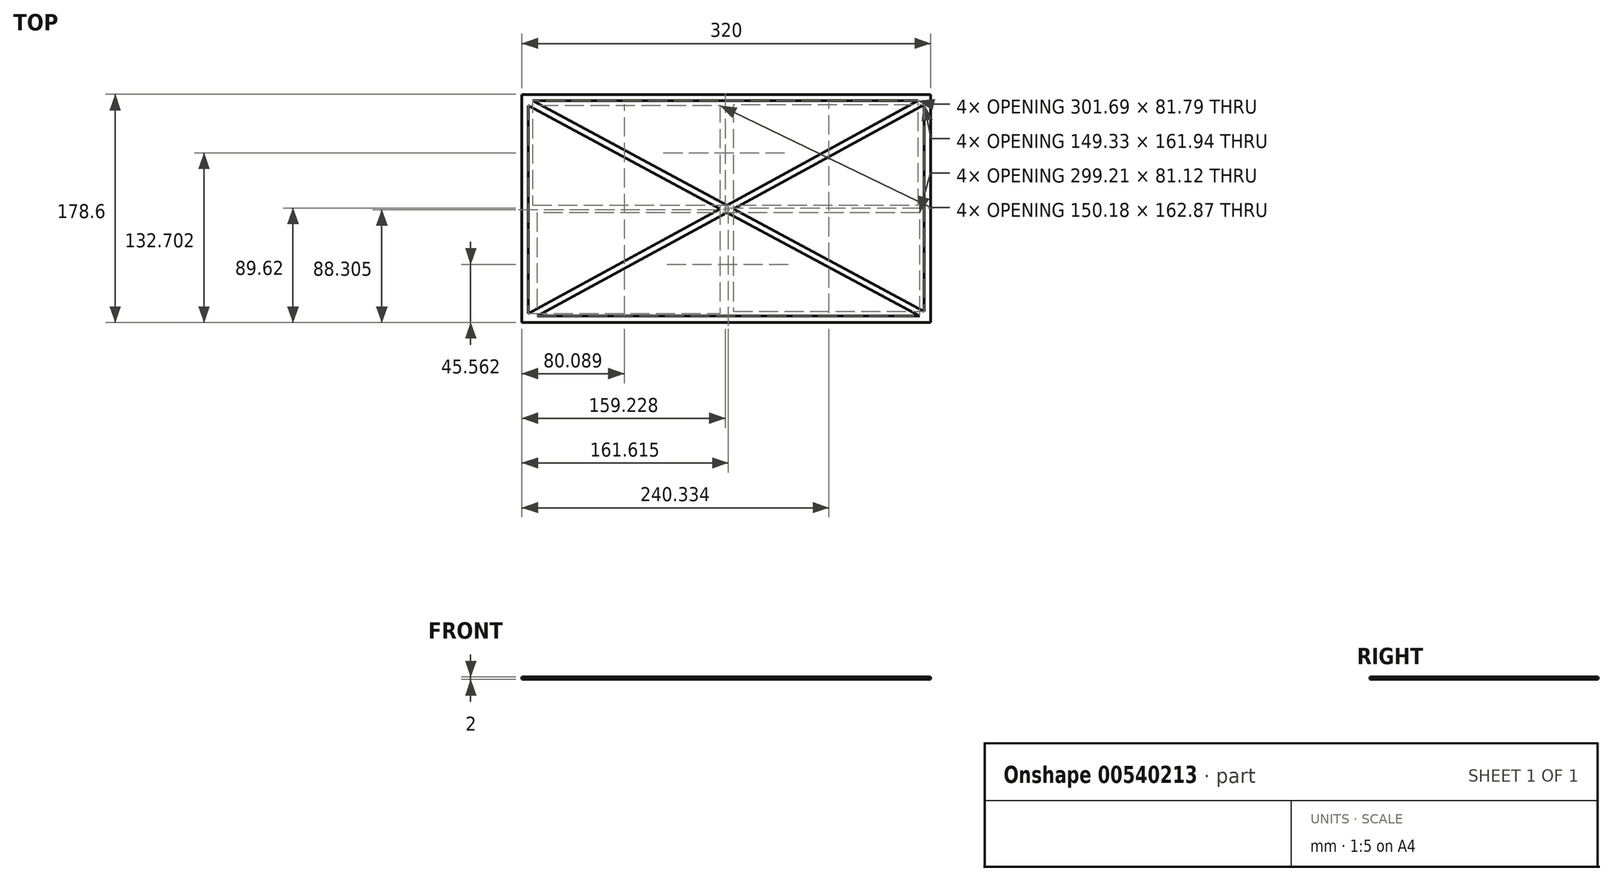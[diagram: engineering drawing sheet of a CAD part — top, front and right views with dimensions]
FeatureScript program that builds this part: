
annotation { "Feature Type Name" : "Feature", "Feature Type Description" : "" }
export const myFeature = defineFeature(function(context is Context, id is Id, definition is map)
    precondition{}
    {
        {
            var Q0;
            Q0=qCreatedBy(makeId("Top.planeOp"),FACE);
            var sketch = newSketch(context, id + "F0", { "sketchPlane" : qUnion([Q0])});
            skLineSegment(sketch, "E0.bottom", {"start": v(-151, 93.56) * mm, "end": v(169, 93.56) * mm});
            skLineSegment(sketch, "E0.top", {"start": v(-151, -85.04) * mm, "end": v(169, -85.04) * mm});
            skLineSegment(sketch, "E0.left", {"start": v(-151, 93.56) * mm, "end": v(-151, -85.04) * mm});
            skLineSegment(sketch, "E0.right", {"start": v(169, 93.56) * mm, "end": v(169, -85.04) * mm});
            skLineSegment(sketch, "E1.bottom", {"start": v(-142.62, 88.56) * mm, "end": v(159.07, 88.56) * mm});
            skLineSegment(sketch, "E1.top", {"start": v(-138.99, -80.04) * mm, "end": v(160.22, -80.04) * mm});
            skLineSegment(sketch, "E1.left", {"start": v(-146, 84.7) * mm, "end": v(-146, -78.17) * mm});
            skLineSegment(sketch, "E1.right", {"start": v(164, 88.56) * mm, "end": v(164, 88.4) * mm});
            skLineSegment(sketch, "E2.bottom", {"start": v(-146, -78.17) * mm, "end": v(4.18, 3.9) * mm});
            skLineSegment(sketch, "E2.top", {"start": v(-138.99, -80.04) * mm, "end": v(9.44, 1.08) * mm});
            skLineSegment(sketch, "E2.right", {"start": v(163.91, 88.56) * mm, "end": v(164, 88.4) * mm});
            skLineSegment(sketch, "E3.bottom", {"start": v(-142.62, 88.56) * mm, "end": v(9.42, 6.77) * mm});
            skLineSegment(sketch, "E3.top", {"start": v(-146, 84.7) * mm, "end": v(4.18, 3.9) * mm});
            skLineSegment(sketch, "E4.trimOffspring", {"start": v(163.91, 88.56) * mm, "end": v(164, 88.56) * mm});
            skLineSegment(sketch, "E5.trimOffspring", {"start": v(164, 85.55) * mm, "end": v(164, -76.4) * mm});
            skLineSegment(sketch, "E6.trimOffspring", {"start": v(9.44, 1.08) * mm, "end": v(160.22, -80.04) * mm});
            skLineSegment(sketch, "E7.trimOffspring", {"start": v(9.42, 6.77) * mm, "end": v(159.07, 88.56) * mm});
            skLineSegment(sketch, "E8.trimOffspring", {"start": v(14.67, 3.94) * mm, "end": v(164, -76.4) * mm});
            skLineSegment(sketch, "E9.trimOffspring", {"start": v(14.67, 3.94) * mm, "end": v(164, 85.55) * mm});
            skSolve(sketch);
        }
        {
            var Q0;
            Q0 = qSketchRegion(id + "F0", true);
            extrude(context, id + "F1", {"entities" : qUnion([Q0]), "depth" : 2 * mm, "offsetDistance" : 25 * mm});
        }
    });
